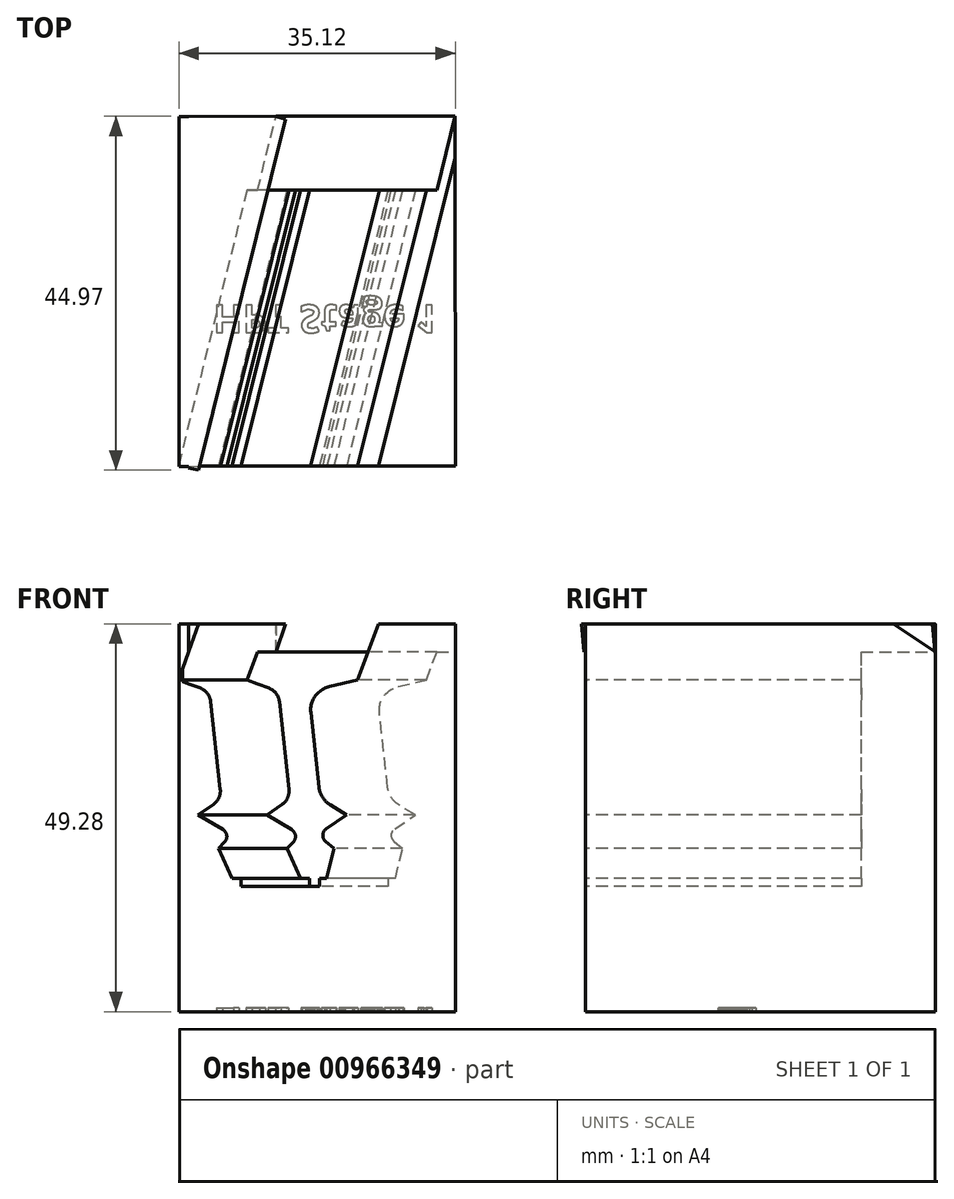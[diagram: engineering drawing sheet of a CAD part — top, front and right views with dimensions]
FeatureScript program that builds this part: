
annotation { "Feature Type Name" : "Feature", "Feature Type Description" : "" }
export const myFeature = defineFeature(function(context is Context, id is Id, definition is map)
    precondition{}
    {
        {
            var Q0;
            Q0=qCreatedBy(makeId("Top.planeOp"),FACE);
            var sketch = newSketch(context, id + "F0", { "sketchPlane" : qUnion([Q0])});
            skLineSegment(sketch, "E0", {"start": v(-14.5, -15.06) * mm, "end": v(-3.44, 29.4) * mm});
            skLineSegment(sketch, "E1", {"start": v(-8.98, 7.16) * mm, "end": v(12.47, 1.83) * mm, "construction": true});
            skLineSegment(sketch, "E2", {"start": v(12.47, 1.83) * mm, "end": v(8.27, -15.06) * mm});
            skLineSegment(sketch, "E3", {"start": v(12.47, 1.83) * mm, "end": v(19.33, 29.4) * mm});
            skLineSegment(sketch, "E4", {"start": v(-14.53, 29.38) * mm, "end": v(19.33, 29.4) * mm});
            skLineSegment(sketch, "E5", {"start": v(-8.98, 7.16) * mm, "end": v(-6.02, 6.43) * mm, "construction": true});
            skLineSegment(sketch, "E6", {"start": v(12.47, 1.83) * mm, "end": v(4.58, 3.79) * mm, "construction": true});
            skLineSegment(sketch, "E7", {"start": v(-14.5, -15.06) * mm, "end": v(19.35, -15.05) * mm});
            skLineSegment(sketch, "E8", {"start": v(19.33, 29.4) * mm, "end": v(19.35, -15.05) * mm});
            skLineSegment(sketch, "E9", {"start": v(19.35, -15.05) * mm, "end": v(19.35, -9.97) * mm, "construction": true});
            skLineSegment(sketch, "E10", {"start": v(19.35, -9.97) * mm, "end": v(9.53, -9.97) * mm, "construction": true});
            skLineSegment(sketch, "E11", {"start": v(9.53, -9.97) * mm, "end": v(-13.24, -9.98) * mm});
            skLineSegment(sketch, "E12", {"start": v(19.33, 29.4) * mm, "end": v(19.33, 20) * mm, "construction": true});
            skLineSegment(sketch, "E13", {"start": v(17, 20) * mm, "end": v(-5.78, 19.99) * mm});
            skLineSegment(sketch, "E14", {"start": v(-6.02, 6.43) * mm, "end": v(-2.64, 20) * mm, "construction": true});
            skLineSegment(sketch, "E15", {"start": v(4.58, 3.79) * mm, "end": v(8.61, 20) * mm, "construction": true});
            skLineSegment(sketch, "E16", {"start": v(-2.64, 20) * mm, "end": v(-0.3, 29.39) * mm});
            skLineSegment(sketch, "E17", {"start": v(8.61, 20) * mm, "end": v(10.95, 29.4) * mm});
            skLineSegment(sketch, "E18", {"start": v(19.35, -9.97) * mm, "end": v(19.34, -2.35) * mm, "construction": true});
            skLineSegment(sketch, "E19", {"start": v(19.34, -2.35) * mm, "end": v(11.43, -2.35) * mm, "construction": true});
            skLineSegment(sketch, "E20", {"start": v(11.43, -2.35) * mm, "end": v(-11.35, -2.36) * mm});
            skLineSegment(sketch, "E21", {"start": v(11.43, -2.35) * mm, "end": v(-10.02, 2.98) * mm});
            skLineSegment(sketch, "E22", {"start": v(17, 20) * mm, "end": v(19.33, 20) * mm});
            skLineSegment(sketch, "E23", {"start": v(-5.78, 19.99) * mm, "end": v(-14.52, 19.99) * mm});
            skLineSegment(sketch, "E24", {"start": v(-15.77, -15.06) * mm, "end": v(-14.5, -15.06) * mm, "construction": true});
            skLineSegment(sketch, "E25", {"start": v(-14.5, -15.06) * mm, "end": v(-15.77, -15.06) * mm});
            skLineSegment(sketch, "E26", {"start": v(-15.77, -15.06) * mm, "end": v(-15.77, 29.38) * mm});
            skLineSegment(sketch, "E27", {"start": v(-15.77, 29.38) * mm, "end": v(-14.53, 29.38) * mm});
            skLineSegment(sketch, "E28", {"start": v(-14.52, 19.99) * mm, "end": v(-15.77, 19.99) * mm});
            skSolve(sketch);
        }
        {
            var Q0;
            {var subQ0=sQuery(id+"F0.wireOp",EDGE,"E23");Q0=makeQuery(id+"F0.imprint","IMPRINT",FACE,{"disambiguationData":[TD([[makeQuery(id+"F0.imprint","IMPRINT",EDGE,{"derivedFrom":subQ0}),1.0]])]});}
            var Q1;
            {var subQ6=sQuery(id+"F0.wireOp",EDGE,"E21");Q1=makeQuery(id+"F0.imprint","IMPRINT",FACE,{"disambiguationData":[TD([[makeQuery(id+"F0.imprint","IMPRINT",EDGE,{"derivedFrom":subQ6}),-1.0]])]});}
            var Q2;
            {var subQ3=sQuery(id+"F0.wireOp",EDGE,"E22");Q2=makeQuery(id+"F0.imprint","IMPRINT",FACE,{"disambiguationData":[TD([[makeQuery(id+"F0.imprint","IMPRINT",EDGE,{"derivedFrom":subQ3}),-1.0]])]});}
            var Q3;
            {var subQ3=sQuery(id+"F0.wireOp",EDGE,"E11");Q3=makeQuery(id+"F0.imprint","IMPRINT",FACE,{"disambiguationData":[TD([[makeQuery(id+"F0.imprint","IMPRINT",EDGE,{"derivedFrom":subQ3}),1.0]])]});}
            var Q4;
            {var subQ0=sQuery(id+"F0.wireOp",EDGE,"E25");Q4=makeQuery(id+"F0.imprint","IMPRINT",FACE,{"disambiguationData":[TD([[makeQuery(id+"F0.imprint","IMPRINT",EDGE,{"derivedFrom":subQ0}),-1.0]])]});}
            extrude(context, id + "F1", {"entities" : qUnion([Q0, Q1, Q2, Q3, Q4]), "oppositeDirection" : true, "depth" : 45.72 * mm, "offsetDistance" : 25.4 * mm});
        }
        {
            var Q0;
            {var subQ0=sQuery(id+"F0.wireOp",EDGE,"E23");Q0=makeQuery(id+"F0.imprint","IMPRINT",FACE,{"disambiguationData":[TD([[makeQuery(id+"F0.imprint","IMPRINT",EDGE,{"derivedFrom":subQ0}),-1.0]])]});}
            var Q1;
            {var subQ0=sQuery(id+"F0.wireOp",EDGE,"E23");Q1=makeQuery(id+"F0.imprint","IMPRINT",FACE,{"disambiguationData":[TD([[makeQuery(id+"F0.imprint","IMPRINT",EDGE,{"derivedFrom":subQ0}),1.0]])]});}
            var Q2;
            {var subQ3=sQuery(id+"F0.wireOp",EDGE,"E22");Q2=makeQuery(id+"F0.imprint","IMPRINT",FACE,{"disambiguationData":[TD([[makeQuery(id+"F0.imprint","IMPRINT",EDGE,{"derivedFrom":subQ3}),1.0]])]});}
            var Q3;
            {var subQ3=sQuery(id+"F0.wireOp",EDGE,"E22");Q3=makeQuery(id+"F0.imprint","IMPRINT",FACE,{"disambiguationData":[TD([[makeQuery(id+"F0.imprint","IMPRINT",EDGE,{"derivedFrom":subQ3}),-1.0]])]});}
            var Q4;
            Q4=makeQuery(id+"F0.imprint","IMPRINT",FACE,{"disambiguationData":[TD([[makeQuery(id+"F0.imprint","IMPRINT",EDGE,{"derivedFrom":sQuery(id+"F0.wireOp",EDGE,"EiXNmNkl-uRiH-0OiR-F0Sd-UMHYAQsNCQRs")}),1.0]])]});
            extrude(context, id + "F2", {"entities" : qUnion([Q0, Q1, Q2, Q3, Q4]), "operationType" : NewBodyOperationType.ADD, "depth" : 3.56 * mm, "offsetDistance" : 25.4 * mm});
        }
        {
            var Q0;
            Q0=makeQuery(id+"F1.opExtrude","SWEPT_FACE",FACE,{"disambiguationData":[OSD([sQuery(id+"F0.wireOp",EDGE,"E21")])]});
            cPlane(context, id + "F3", {"entities" : qUnion([Q0]), "cplaneType" : CPlaneType.OFFSET, "offset" : 18.8 * mm, "width" : 152.4 * mm, "height" : 152.4 * mm});
        }
        {
            var Q0;
            Q0=qCreatedBy(id+"F3.planeOp",FACE);
            var sketch = newSketch(context, id + "F4", { "sketchPlane" : qUnion([Q0])});
            skLineSegment(sketch, "E29", {"start": v(-15.4, 0) * mm, "end": v(-15.4, -0.01) * mm, "construction": true});
            skLineSegment(sketch, "E30", {"start": v(-10.44, 0) * mm, "end": v(11.66, 0) * mm});
            skLineSegment(sketch, "E31", {"start": v(-2.31, 0) * mm, "end": v(0.79, -29.46) * mm, "construction": true});
            skLineSegment(sketch, "E32", {"start": v(11.66, 0) * mm, "end": v(10.36, -3.55) * mm});
            skLineSegment(sketch, "E33", {"start": v(10.36, -3.55) * mm, "end": v(11.66, 0) * mm});
            skLineSegment(sketch, "E34", {"start": v(11.66, 0) * mm, "end": v(12.95, 3.56) * mm});
            skLineSegment(sketch, "E35", {"start": v(12.95, 3.56) * mm, "end": v(11.66, 3.56) * mm});
            skLineSegment(sketch, "E36", {"start": v(11.66, 3.56) * mm, "end": v(11.66, 0) * mm});
            skLineSegment(sketch, "E37", {"start": v(-10.44, 0) * mm, "end": v(-11.73, -3.56) * mm});
            skLineSegment(sketch, "E38", {"start": v(-10.44, 0) * mm, "end": v(-10.44, 3.56) * mm});
            skLineSegment(sketch, "E39", {"start": v(-10.44, 3.56) * mm, "end": v(-9.15, 3.56) * mm});
            skLineSegment(sketch, "E40", {"start": v(-10.44, 0) * mm, "end": v(-9.15, 3.56) * mm});
            skLineSegment(sketch, "E41", {"start": v(5.75, -18.7) * mm, "end": v(9.01, -20.71) * mm});
            skPoint(sketch, "E42.end.orphan", {"position": v(-10.44, -3.56) * mm});
            skLineSegment(sketch, "E43", {"start": v(-9.28, -20.71) * mm, "end": v(-5.2, -23.24) * mm});
            skLineSegment(sketch, "E44", {"start": v(9.01, -20.71) * mm, "end": v(5.47, -23.24) * mm});
            skLineSegment(sketch, "E45", {"start": v(-6.8, -25) * mm, "end": v(-5.2, -23.24) * mm});
            skLineSegment(sketch, "E46", {"start": v(7.43, -25) * mm, "end": v(5.47, -23.24) * mm});
            skLineSegment(sketch, "E47", {"start": v(5.75, -18.7) * mm, "end": v(-0.34, -18.7) * mm, "construction": true});
            skLineSegment(sketch, "E48", {"start": v(-0.34, -18.7) * mm, "end": v(-6.44, -18.7) * mm, "construction": true});
            skLineSegment(sketch, "E49", {"start": v(9.01, -20.71) * mm, "end": v(-0.13, -20.71) * mm, "construction": true});
            skLineSegment(sketch, "E50", {"start": v(-0.13, -20.71) * mm, "end": v(-9.28, -20.71) * mm, "construction": true});
            skLineSegment(sketch, "E51", {"start": v(-9.28, -20.71) * mm, "end": v(-6.44, -18.7) * mm});
            skLineSegment(sketch, "E52", {"start": v(5.47, -23.24) * mm, "end": v(0.13, -23.24) * mm, "construction": true});
            skLineSegment(sketch, "E53", {"start": v(0.13, -23.24) * mm, "end": v(-5.2, -23.24) * mm, "construction": true});
            skLineSegment(sketch, "E54", {"start": v(7.43, -25) * mm, "end": v(0.32, -25) * mm, "construction": true});
            skLineSegment(sketch, "E55", {"start": v(0.32, -25) * mm, "end": v(-6.8, -25) * mm, "construction": true});
            skLineSegment(sketch, "E56", {"start": v(0.72, -28.8) * mm, "end": v(0.79, -29.46) * mm, "construction": true});
            skLineSegment(sketch, "E57", {"start": v(0.72, -28.8) * mm, "end": v(6.56, -28.8) * mm, "construction": true});
            skLineSegment(sketch, "E58", {"start": v(0.72, -28.8) * mm, "end": v(-5.12, -28.8) * mm, "construction": true});
            skLineSegment(sketch, "E59", {"start": v(-6.8, -25) * mm, "end": v(-5.12, -28.8) * mm});
            skLineSegment(sketch, "E60", {"start": v(7.43, -25) * mm, "end": v(6.56, -28.8) * mm});
            skLineSegment(sketch, "E61", {"start": v(0.72, -28.8) * mm, "end": v(0.83, -29.8) * mm, "construction": true});
            skLineSegment(sketch, "E62", {"start": v(0.83, -29.8) * mm, "end": v(5.65, -29.8) * mm, "construction": true});
            skLineSegment(sketch, "E63", {"start": v(0.83, -29.8) * mm, "end": v(-4, -29.8) * mm, "construction": true});
            skLineSegment(sketch, "E64", {"start": v(-4, -29.8) * mm, "end": v(0.83, -29.8) * mm});
            skLineSegment(sketch, "E65", {"start": v(0.83, -29.8) * mm, "end": v(5.65, -29.8) * mm});
            skLineSegment(sketch, "E66", {"start": v(5.65, -29.8) * mm, "end": v(5.65, -28.8) * mm});
            skLineSegment(sketch, "E67", {"start": v(5.65, -28.8) * mm, "end": v(6.56, -28.8) * mm});
            skLineSegment(sketch, "E68", {"start": v(-4, -29.8) * mm, "end": v(-4, -28.8) * mm});
            skLineSegment(sketch, "E69", {"start": v(-4, -28.8) * mm, "end": v(-5.12, -28.8) * mm});
            skLineSegment(sketch, "E70", {"start": v(1.16, 0) * mm, "end": v(1.16, -5.08) * mm, "construction": true});
            skLineSegment(sketch, "E71", {"start": v(-1.78, -5.08) * mm, "end": v(4.32, -5.08) * mm, "construction": true});
            skLineSegment(sketch, "E72", {"start": v(-1.78, -5.08) * mm, "end": v(-7.87, -5.08) * mm, "construction": true});
            skLineSegment(sketch, "E73", {"start": v(-11.73, -3.56) * mm, "end": v(-7.87, -5.08) * mm});
            skLineSegment(sketch, "E74", {"start": v(10.36, -3.55) * mm, "end": v(4.32, -5.08) * mm});
            skLineSegment(sketch, "E75", {"start": v(4.32, -5.08) * mm, "end": v(5.75, -18.7) * mm});
            skLineSegment(sketch, "E76", {"start": v(-7.87, -5.08) * mm, "end": v(-6.44, -18.7) * mm});
            skSolve(sketch);
        }
        {
            var Q0;
            {var subQ0=sQuery(id+"F0.wireOp",EDGE,"E20");Q0=makeQuery(id+"F0.imprint","IMPRINT",FACE,{"disambiguationData":[TD([[makeQuery(id+"F0.imprint","IMPRINT",EDGE,{"derivedFrom":subQ0}),-1.0]])]});}
            var Q1;
            {var subQ0=sQuery(id+"F0.wireOp",EDGE,"E11");Q1=makeQuery(id+"F0.imprint","IMPRINT",FACE,{"disambiguationData":[TD([[makeQuery(id+"F0.imprint","IMPRINT",EDGE,{"derivedFrom":subQ0}),-1.0]])]});}
            extrude(context, id + "F5", {"entities" : qUnion([Q0, Q1]), "operationType" : NewBodyOperationType.ADD, "oppositeDirection" : true, "depth" : 45.72 * mm, "offsetDistance" : 25.4 * mm});
        }
        {
            var Q0;
            Q0=makeQuery(id+"F4.imprint","IMPRINT",FACE,{"disambiguationData":[TD([[makeQuery(id+"F4.imprint","IMPRINT",EDGE,{"derivedFrom":sQuery(id+"F4.wireOp",EDGE,"E30")}),-1.0]])]});
            extrude(context, id + "F6", {"entities" : qUnion([Q0]), "operationType" : NewBodyOperationType.REMOVE, "oppositeDirection" : true, "depth" : 43.18 * mm, "offsetDistance" : 25.4 * mm});
        }
        {
            var Q0;
            Q0=makeQuery(id+"F4.imprint","IMPRINT",FACE,{"disambiguationData":[TD([[makeQuery(id+"F4.imprint","IMPRINT",EDGE,{"derivedFrom":sQuery(id+"F4.wireOp",EDGE,"E34")}),1.0]])]});
            extrude(context, id + "F7", {"entities" : qUnion([Q0]), "operationType" : NewBodyOperationType.REMOVE, "oppositeDirection" : true, "depth" : 53.34 * mm, "offsetDistance" : 25.4 * mm});
        }
        {
            var Q0;
            Q0=makeQuery(id+"F4.imprint","IMPRINT",FACE,{"disambiguationData":[TD([[makeQuery(id+"F4.imprint","IMPRINT",EDGE,{"derivedFrom":sQuery(id+"F4.wireOp",EDGE,"E38")}),-1.0]])]});
            extrude(context, id + "F8", {"entities" : qUnion([Q0]), "operationType" : NewBodyOperationType.ADD, "oppositeDirection" : true, "depth" : 45.97 * mm, "offsetDistance" : 25.4 * mm});
        }
        {
            var Q0;
            Q0=makeQuery(id+"F6.boolean.opBoolean","COPY",EDGE,{"derivedFrom":makeQuery(id+"F6.opExtrude","SWEPT_EDGE",EDGE,{"disambiguationData":[OSD([sQuery(id+"F4.wireOp",EDGE,"E44"),sQuery(id+"F4.wireOp",EDGE,"E46")])]})});
            var Q1;
            Q1=makeQuery(id+"F6.boolean.opBoolean","COPY",EDGE,{"derivedFrom":makeQuery(id+"F6.opExtrude","SWEPT_EDGE",EDGE,{"disambiguationData":[OSD([sQuery(id+"F4.wireOp",EDGE,"E43"),sQuery(id+"F4.wireOp",EDGE,"E45")])]})});
            fillet(context, id + "F9", {"entities" : qUnion([Q0, Q1]), "radius" : 1.02 * mm, "tangentPropagation" : true, "defaultsChanged" : false, "vertexSettings" : [], "allowEdgeOverflow" : false});
        }
        {
            var Q0;
            Q0=makeQuery(id+"F6.boolean.opBoolean","COPY",EDGE,{"derivedFrom":makeQuery(id+"F6.opExtrude","SWEPT_EDGE",EDGE,{"disambiguationData":[OSD([sQuery(id+"F4.wireOp",EDGE,"E73"),sQuery(id+"F4.wireOp",EDGE,"E76")])]})});
            var Q1;
            Q1=makeQuery(id+"F6.boolean.opBoolean","COPY",EDGE,{"derivedFrom":makeQuery(id+"F6.opExtrude","SWEPT_EDGE",EDGE,{"disambiguationData":[OSD([sQuery(id+"F4.wireOp",EDGE,"E51"),sQuery(id+"F4.wireOp",EDGE,"E76")])]})});
            fillet(context, id + "F10", {"entities" : qUnion([Q0, Q1]), "tangentPropagation" : true, "radius" : 2.03 * mm, "defaultsChanged" : false, "vertexSettings" : [], "allowEdgeOverflow" : false});
        }
        {
            var Q0;
            Q0=makeQuery(id+"F6.boolean.opBoolean","COPY",EDGE,{"derivedFrom":makeQuery(id+"F6.opExtrude","SWEPT_EDGE",EDGE,{"disambiguationData":[OSD([sQuery(id+"F4.wireOp",EDGE,"E74"),sQuery(id+"F4.wireOp",EDGE,"E75")])]})});
            var Q1;
            Q1=makeQuery(id+"F6.boolean.opBoolean","COPY",EDGE,{"derivedFrom":makeQuery(id+"F6.opExtrude","SWEPT_EDGE",EDGE,{"disambiguationData":[OSD([sQuery(id+"F4.wireOp",EDGE,"E41"),sQuery(id+"F4.wireOp",EDGE,"E75")])]})});
            fillet(context, id + "F11", {"entities" : qUnion([Q0, Q1]), "tangentPropagation" : true, "radius" : 3.05 * mm, "defaultsChanged" : true, "vertexSettings" : [], "allowEdgeOverflow" : false});
        }
        {
            var Q0;
            {var subQ0=sQuery(id+"F0.wireOp",EDGE,"E23");Q0=makeQuery(id+"F0.imprint","IMPRINT",FACE,{"disambiguationData":[TD([[makeQuery(id+"F0.imprint","IMPRINT",EDGE,{"derivedFrom":subQ0}),-1.0]])]});}
            var Q1;
            {var subQ5=sQuery(id+"F0.wireOp",EDGE,"E16");Q1=makeQuery(id+"F0.imprint","IMPRINT",FACE,{"disambiguationData":[TD([[makeQuery(id+"F0.imprint","IMPRINT",EDGE,{"derivedFrom":subQ5}),1.0]])]});}
            var Q2;
            {var subQ0=sQuery(id+"F0.wireOp",EDGE,"E16");Q2=makeQuery(id+"F0.imprint","IMPRINT",FACE,{"disambiguationData":[TD([[makeQuery(id+"F0.imprint","IMPRINT",EDGE,{"derivedFrom":subQ0}),-1.0]])]});}
            var Q3;
            {var subQ5=sQuery(id+"F0.wireOp",EDGE,"E17");Q3=makeQuery(id+"F0.imprint","IMPRINT",FACE,{"disambiguationData":[TD([[makeQuery(id+"F0.imprint","IMPRINT",EDGE,{"derivedFrom":subQ5}),-1.0]])]});}
            var Q4;
            {var subQ3=sQuery(id+"F0.wireOp",EDGE,"E22");Q4=makeQuery(id+"F0.imprint","IMPRINT",FACE,{"disambiguationData":[TD([[makeQuery(id+"F0.imprint","IMPRINT",EDGE,{"derivedFrom":subQ3}),1.0]])]});}
            var Q5;
            Q5=makeQuery(id+"F0.imprint","IMPRINT",FACE,{"disambiguationData":[TD([[makeQuery(id+"F0.imprint","IMPRINT",EDGE,{"derivedFrom":sQuery(id+"F0.wireOp",EDGE,"EiXNmNkl-uRiH-0OiR-F0Sd-UMHYAQsNCQRs")}),1.0]])]});
            extrude(context, id + "F12", {"entities" : qUnion([Q0, Q1, Q2, Q3, Q4, Q5]), "operationType" : NewBodyOperationType.ADD, "oppositeDirection" : true, "depth" : 45.72 * mm, "offsetDistance" : 25.4 * mm});
        }
        {
            var Q0;
            {var subQ0=sQuery(id+"F0.wireOp",EDGE,"E13");var subQ1=sQuery(id+"F0.wireOp",EDGE,"E4");var subQ2=sQuery(id+"F0.wireOp",EDGE,"E3");var subQ3=sQuery(id+"F0.wireOp",EDGE,"E0");var subQ4=sQuery(id+"F0.wireOp",EDGE,"E21");var subQ5=sQuery(id+"F0.wireOp",EDGE,"E11");var subQ6=sQuery(id+"F0.wireOp",EDGE,"E2");Q0=makeQuery(id+"F12.boolean.opBoolean","MERGE",FACE,{"derivedFrom":[makeQuery(id+"F5.boolean.opBoolean","MERGE",FACE,{"derivedFrom":[makeQuery(id+"F1.opExtrude","CAP_FACE",FACE,{"disambiguationData":[OSD([subQ3,sQuery(id+"F0.wireOp",EDGE,"EiXNmNkl-uRiH-0OiR-F0Sd-UMHYAQsNCQRs"),subQ6,subQ2,subQ1,sQuery(id+"F0.wireOp",EDGE,"E7"),sQuery(id+"F0.wireOp",EDGE,"E8"),subQ5,subQ0,subQ4])],"isStart":false}),makeQuery(id+"F5.opExtrude","CAP_FACE",FACE,{"disambiguationData":[OSD([subQ3,subQ6,subQ5,subQ4])],"isStart":false})]}),makeQuery(id+"F12.opExtrude","CAP_FACE",FACE,{"disambiguationData":[OSD([subQ3,subQ2,subQ1,subQ0])],"isStart":false})]});}
            var sketch = newSketch(context, id + "F13", { "sketchPlane" : qUnion([Q0])});
            skText(sketch, "E77", { "text": "HPT Stage 1", "fontName": "OpenSans-Bold.ttf"});
            const initialGuessF13  = {"E77": [-0.01142, -0.00541, 1, 0, 0.00354]};
            skSetInitialGuess(sketch, initialGuessF13);
            skSolve(sketch);
        }
        {
            var Q0;
            Q0=qSketchRegion(id+"F13",true);
            var Q1;
            Q1=qConstructionFilter(qBodyType(qCreatedBy(id+"F13",EDGE),BodyType.WIRE),ConstructionObject.NO);
            extrude(context, id + "F14", {"entities" : qUnion([Q0]), "operationType" : NewBodyOperationType.REMOVE, "surfaceEntities" : qUnion([Q1]), "oppositeDirection" : true, "depth" : 0.5 * mm, "offsetDistance" : 25.4 * mm});
        }
    });
